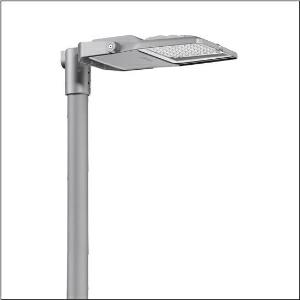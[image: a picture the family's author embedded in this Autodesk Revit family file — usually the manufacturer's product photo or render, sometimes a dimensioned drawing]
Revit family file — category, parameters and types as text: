
# Revit family: floodlight_fl_21_mini___pl33t_5xa7775c2f3a_8bfe
name_source: partatom
category: Lighting Fixtures
units: mm (PartAtom-declared; Revit-internal decimal feet)

## family parameters
Cut with Voids When Loaded = No
Host = Face
Light Source = No
Part Type = Normal
Room Calculation Point = No
Round Connector Dimension = Use Diameter
Shared = No

## types (1)
- --- (1 x LED, 12050 lm, 89 W, 3000K)
    Apparent Load = 89 VA
    CIE Flux Codes = 26 75 99 100 100
    Color Rendering = 70
    Color Temperature = 3000K
    Default Elevation = 1800 mm
    Description = Floodlight FL 21 mini, floodlight, primary light control with lens, of PMMA, primary optical cover: protective disc, of toughened safety glass, transparent, light distribution: PL33T, light emission: direct distribution, installation type: surface-mounted, LED, High Power LED, rated luminous flux: 12.050lm, luminous efficacy: 135lm/W, light colour: 730, colour temperature: 3000K, control: flexible luminous flux parameterisation, time-dependent luminous flux control, constant luminous flux control, overheat protection, presetting dimming logarithmic, with terminal, 6-pole, mains connection: 220..240V, AC, 50/60Hz, start of lifetime: 89W, end of service life: 94W, reduction: 43W, luminaire housing, of diecast aluminium, powder-coated, Siteco® metallic grey (DB 702S), corrosivity category C5 mid according to DIN EN ISO 12944, sealing non-destructively replaceable, please order mast flange separately, mast bracket, of steel, galvanised, powder-coated, Siteco® metallic grey (DB 702S), Smart Interface above, protection rating (complete): IP66, insulation class (complete): insulation class II (safety insulation), certification: CE, ENEC, VDE, protection symbol: D, impact resistance: IK08, permissible operating ambient temperature: -40..+40°C, permissible operating ambient temperature for outdoor applications: -40..+50°C, standard: DIN EN 12944, LABS conformity tested according to VDMA 24364:2018-05, packaging unit: 1 piece

Light Distribution: PL33T
    Height = 70 mm
    Lamp = 1 x LED
    Lamp Light Flux = 12050 lm
    Lamp Power = 89 W
    Lamp count = 1
    Length = 485 mm
    Luminous efficacy = 135 lm/W
    Manufacturer = Siteco
    ModVariant = No
    Model = 5XA7775C2F3A
    Number of Poles = 1
    OnlyDefault = Yes
    Power Factor = 1
    Product Name = Floodlight FL 21 mini | PL33T
    Product group = floodlight | pylon annexe
    ProductGroupID = 6200
    Protection Class = Protection class II
    Protection Degree = IP 66
    RLX_Detail_Level = 1
    RLX_Emergency_Light_Flux = 0 lm
    RLX_Emergency_Type = 0
    RLX_Emergency_Type_DB = No
    RlxData = <blob elided: 100653 chars, md5=83948eee>
    Socket = socket
    Standby Power = 0 W
    System Light Flux = 12050 lm
    System Power = 89 W
    Type Comments = factory setting: luminous flux: 100 % | dim-lin: 254 | 456 mA
    Type Image = l_1007125.jpg
    URL = http://relux.com
    VarID = @adj_098699
    Voltage = 0 V
    Weight = 0.00 kg
    Width = 337 mm

## geometry (parser evidence)
native form markers: Blend x4, Sweep x12
no freeform markers — native parametric forms only
